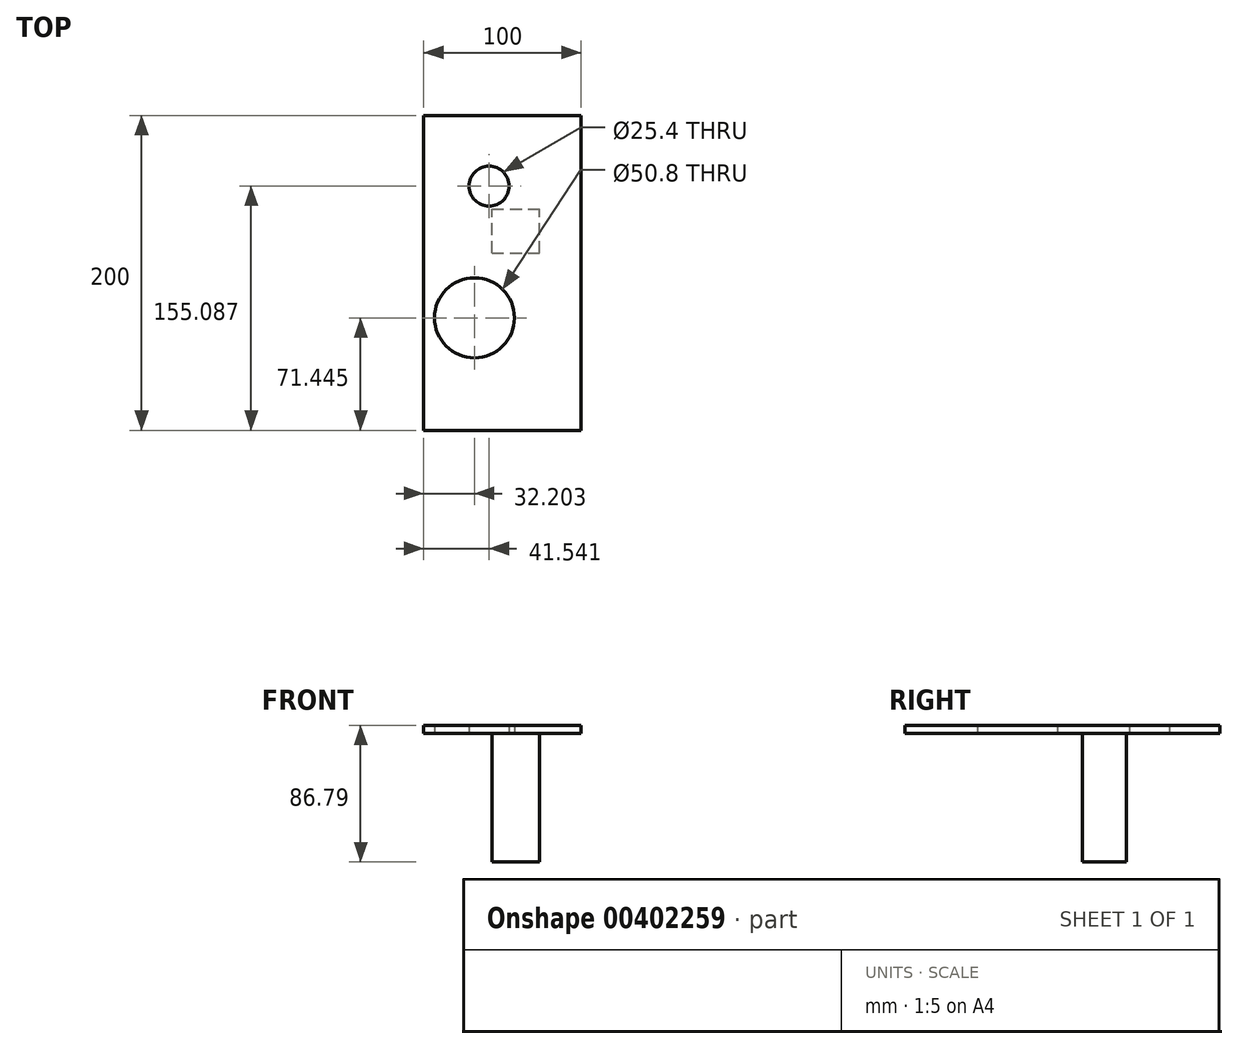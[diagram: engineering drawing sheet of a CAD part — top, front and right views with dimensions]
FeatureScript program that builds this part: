
annotation { "Feature Type Name" : "Feature", "Feature Type Description" : "" }
export const myFeature = defineFeature(function(context is Context, id is Id, definition is map)
    precondition{}
    {
        {
            var Q0;
            Q0=qCreatedBy(makeId("Top.planeOp"),FACE);
            var sketch = newSketch(context, id + "F0", { "sketchPlane" : qUnion([Q0])});
            skLineSegment(sketch, "E0.bottom", {"start": v(0, 0) * mm, "end": v(100, 0) * mm});
            skLineSegment(sketch, "E0.top", {"start": v(0, 200) * mm, "end": v(100, 200) * mm});
            skLineSegment(sketch, "E0.left", {"start": v(0, 0) * mm, "end": v(0, 200) * mm});
            skLineSegment(sketch, "E0.right", {"start": v(100, 0) * mm, "end": v(100, 200) * mm});
            skCircle(sketch, "E1", {"center": v(41.54, 155.09) * mm, "radius": 12.7 * mm});
            skCircle(sketch, "E2", {"center": v(32.2, 71.44) * mm, "radius": 25.4 * mm});
            skSolve(sketch);
        }
        {
            var Q0;
            Q0=makeQuery(id+"F0.imprint","IMPRINT",FACE,{"disambiguationData":[TD([[makeQuery(id+"F0.imprint","IMPRINT",EDGE,{"derivedFrom":sQuery(id+"F0.wireOp",EDGE,"E0.bottom")}),1.0]])]});
            extrude(context, id + "F1", {"entities" : qUnion([Q0]), "depth" : 5 * mm});
        }
        {
            var Q0;
            Q0=makeQuery(id+"F1.opExtrude","CAP_FACE",FACE,{"disambiguationData":[OSD([sQuery(id+"F0.wireOp",EDGE,"E0.bottom"),sQuery(id+"F0.wireOp",EDGE,"E0.top"),sQuery(id+"F0.wireOp",EDGE,"E0.left"),sQuery(id+"F0.wireOp",EDGE,"E0.right"),sQuery(id+"F0.wireOp",EDGE,"E1"),sQuery(id+"F0.wireOp",EDGE,"E2")])],"isStart":true});
            var sketch = newSketch(context, id + "F2", { "sketchPlane" : qUnion([Q0])});
            skLineSegment(sketch, "E3.bottom", {"start": v(43.28, -112.58) * mm, "end": v(73.42, -112.58) * mm});
            skLineSegment(sketch, "E3.top", {"start": v(43.28, -140.42) * mm, "end": v(73.42, -140.42) * mm});
            skLineSegment(sketch, "E3.left", {"start": v(43.28, -112.58) * mm, "end": v(43.28, -140.42) * mm});
            skLineSegment(sketch, "E3.right", {"start": v(73.42, -112.58) * mm, "end": v(73.42, -140.42) * mm});
            skSolve(sketch);
        }
        {
            var Q0;
            Q0=makeQuery(id+"F2.imprint","IMPRINT",FACE,{"disambiguationData":[TD([[makeQuery(id+"F2.imprint","IMPRINT",EDGE,{"derivedFrom":sQuery(id+"F2.wireOp",EDGE,"E3.bottom")}),-1.0]])]});
            extrude(context, id + "F3", {"entities" : qUnion([Q0]), "operationType" : NewBodyOperationType.ADD, "depth" : 81.8 * mm});
        }
    });
